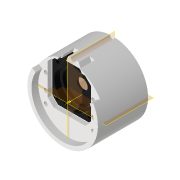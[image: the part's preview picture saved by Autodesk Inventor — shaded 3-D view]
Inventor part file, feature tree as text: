
AUTODESK INVENTOR PART (.ipt)
format: ipt  version: 2022 (Build 260153000, 153)  size: 390,656 bytes
history: native  units: mm
features: reference x20, sketch x7, other x7, extrude x6, plane x3, projected_geometry x3, hole x1
ambient origin geometry x8: Origin, YZ Plane, XZ Plane, XY Plane, X Axis, Y Axis, Z Axis, Center Point
bodies: Volumenkörper1 (feature_tree)
feature tree (47):
  extrude  "Extrusion1"  Depth=2.8mm
  sketch  "Skizze3"  dims[d2=8.0mm d3=0.0mm d4=0.5mm]
  plane  "Arbeitsebene1"
  extrude  "Extrusion2"  Depth=0.5mm
  extrude  "Extrusion3"  Depth=0.5mm
  hole  "Bohrung1"  [1 undecoded]
  extrude  "Extrusion5"  Depth=23.0mm
  other  "Arbeitspunkt1"
  plane  "Arbeitsebene2"
  plane  "Arbeitsebene3"
  extrude  "Extrusion6"  Depth=5.0mm
  extrude  "Extrusion7"  Depth=5.0mm TaperAngle=0.0deg
  sketch  "Skizze1"  dims[d0=2.8mm d1=2.8mm]
  reference  "Referenz1"
  reference  "Referenz2"
  reference  "Referenz3"
  reference  "Referenz4"
  reference  "Referenz5"
  reference  "Referenz7"
  reference  "Referenz8"
  reference  "Referenz9"
  reference  "Referenz10"
  reference  "Referenz11"
  reference  "Referenz12"
  reference  "Referenz13"
  reference  "Referenz14"
  reference  "Referenz15"
  reference  "Referenz16"
  reference  "Referenz17"
  reference  "Referenz18"
  reference  "Referenz19"
  sketch  "Skizze4"  dims[d5=0.5mm d6=0.5mm]
  projected_geometry  "Projizierte Kontur3"
  sketch  "Skizze5"  dims[d7=0.5mm d8=21.0mm d9=0.0mm]
  reference  "Referenz20"
  sketch  "Skizze7"  dims[d10=10.0mm d11=0.0mm]
  reference  "Referenz21"
  projected_geometry  "Projizierte Kontur5"
  other  "Arbeitsachse1"
  sketch  "Skizze8"  dims[d12=2.8mm d13=6.0mm d14=6.5mm d15=23.0mm d16=90.0deg d17=15.0mm d18=20.594885mm d22=0.5mm]
  projected_geometry  "Projizierte Kontur6"
  sketch  "Skizze9"  dims[d23=3.0mm d24=0.0mm d25=46.0mm d26=5.0mm d27=0.0mm d28=4.0mm d29=0.0mm d30=0.0mm]
  other  "MeshFeature1"
  other  "Planktoscope_Mini_Peristalticpump.iam"
  other  "00_Stepper_Motor_28BYJ-48:1"
  other  "Matchboxscope_bottom_v0:1"
  other  "Pump_Lid:1"
note: 1 required parameter value undecoded (feature->parameter linkage not recoverable at this tier; creation-order binding heuristic only, values carry confidence <= 0.55)
